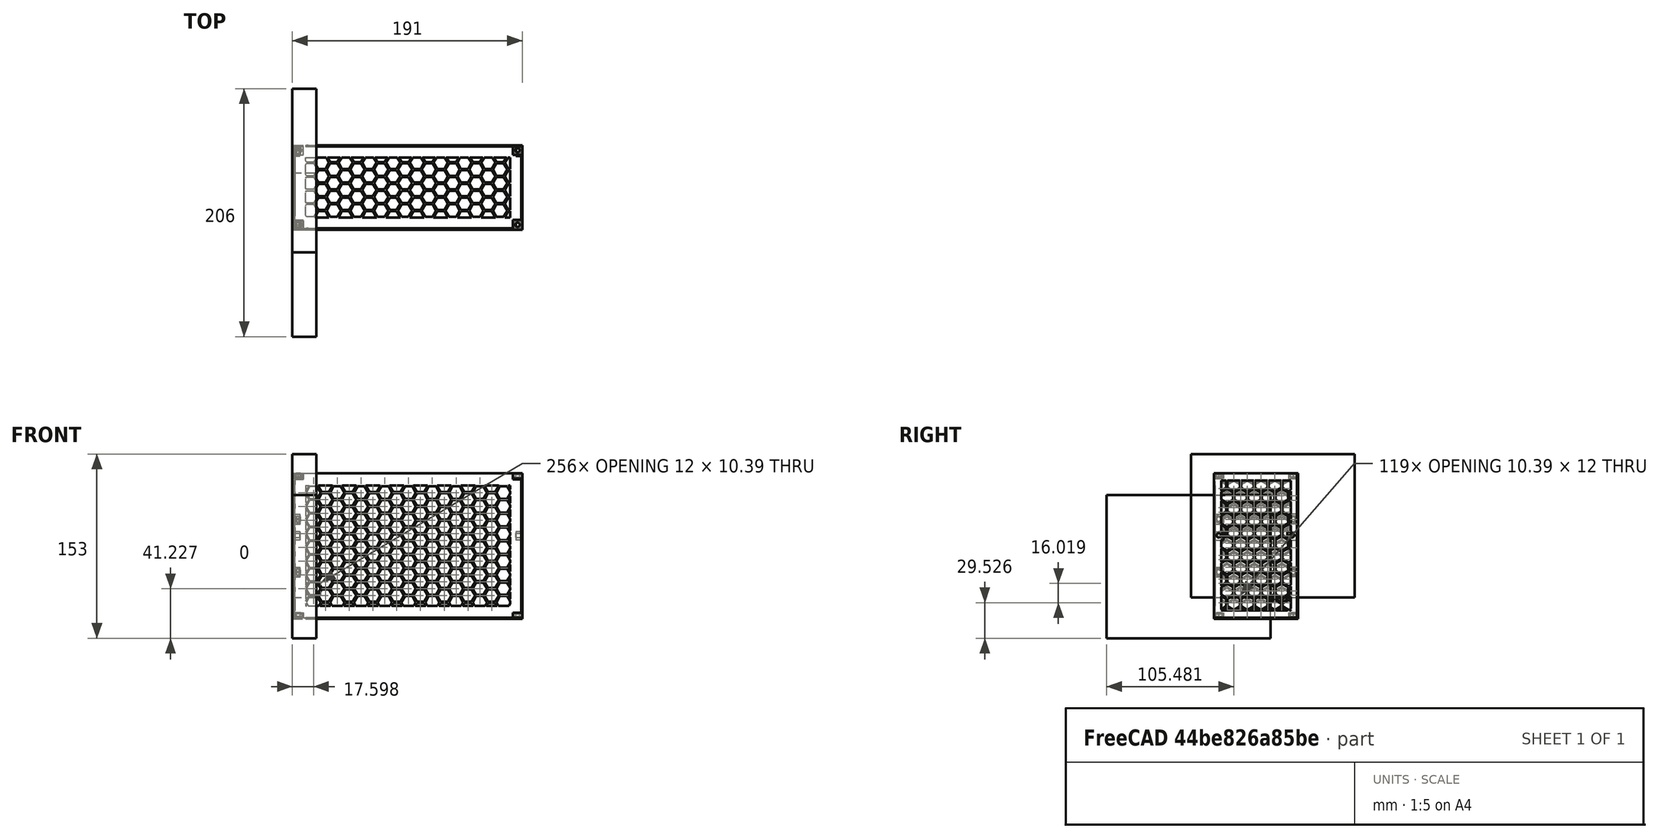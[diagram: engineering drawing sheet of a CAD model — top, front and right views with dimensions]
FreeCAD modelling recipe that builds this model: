
FCSTD DOCUMENT  (FreeCAD 0.18R4 (GitTag))
Label: tapas
License: All rights reserved
LicenseURL: http://en.wikipedia.org/wiki/All_rights_reserved
objects: Part::Box×56, Part::Cut×56, Part::MultiFuse×28, Part::Cylinder×25, Part::Prism×12, Part::Feature×9, Part::MultiCommon×3
note: 189 computed .brp shape members not serialized (recipe doc carries the construction recipe); baked Part::Feature solids carry a one-line shape summary decoded from their .brp

FEATURE [Part::Box] Box031  label="placa002"
  AttacherType = Attacher::AttachEngine3D
  Height = 108
  Length = 1
  Placement = pos=(-89,25,-221) rot=(0,0,1;0rad)
  Width = 58
FEATURE [Part::Box] Box032  label="placa003"
  AttacherType = Attacher::AttachEngine3D
  Height = 108
  Length = 1
  Placement = pos=(-89,25,-221) rot=(0,0,1;0rad)
  Width = 58
FEATURE [Part::Box] Box021  label="Cube017"
  AttacherType = Attacher::AttachEngine3D
  Height = 4.2
  Length = 7
  Placement = pos=(-88,81,-111.2) rot=(0,0,1;0rad)
  Width = 8
FEATURE [Part::Prism] Prism003
  AttacherType = Attacher::AttachEngine3D
  Circumradius = 3.1
  Height = 2.2
  Placement = pos=(-85,85,-110.2) rot=(0,0,1;0rad)
  Polygon = 6
FEATURE [Part::Prism] Prism002
  AttacherType = Attacher::AttachEngine3D
  Circumradius = 3.1
  Height = 2.2
  Placement = pos=(-85,85,-110.2) rot=(0,0,1;0rad)
  Polygon = 6
FEATURE [Part::Box] Box017  label="izquierda"
  AttacherType = Attacher::AttachEngine3D
  Height = 120
  Length = 1
  Placement = pos=(-89,19,-227) rot=(0,0,1;0rad)
  Width = 70
FEATURE [Part::Box] Box030  label="placa1"
  AttacherType = Attacher::AttachEngine3D
  Height = 120
  Length = 1
  Placement = pos=(-89,19,-227) rot=(0,0,1;0rad)
  Width = 70
FEATURE [Part::Prism] Prism001
  AttacherType = Attacher::AttachEngine3D
  Circumradius = 3.4
  Height = 2.4
  Placement = pos=(-85,23,-110.2) rot=(0,0,1;0.523599rad)
  Polygon = 6
FEATURE [Part::Cut] Cut001001001002003001008002002033001001001001001001001002001001002001045002003017008007002010007002014003017024
  Base = -> Box030
  Tool = -> Box032
FEATURE [Part::Box] Box020  label="Cube016"
  AttacherType = Attacher::AttachEngine3D
  Height = 4.2
  Length = 7
  Placement = pos=(-88,19,-111.2) rot=(0,0,1;0rad)
  Width = 8
FEATURE [Part::Box] Box033  label="corta_medio"
  AttacherType = Attacher::AttachEngine3D
  Height = 108
  Length = 1
  Placement = pos=(-89,25,-221) rot=(0,0,1;0rad)
  Width = 58
FEATURE [Part::Box] Box023  label="Cube019"
  AttacherType = Attacher::AttachEngine3D
  Height = 4.2
  Length = 7
  Placement = pos=(-88,19,-111.2) rot=(0,0,1;0rad)
  Width = 8
FEATURE [Part::Box] Box022  label="Cube018"
  AttacherType = Attacher::AttachEngine3D
  Height = 4.2
  Length = 7
  Placement = pos=(-88,81,-111.2) rot=(0,0,1;0rad)
  Width = 8
FEATURE [Part::Prism] Prism004
  AttacherType = Attacher::AttachEngine3D
  Circumradius = 3.1
  Height = 2.2
  Placement = pos=(-85,23,-110.2) rot=(0,0,1;0rad)
  Polygon = 6
FEATURE [Part::Cylinder] Cylinder013
  Angle = 360
  AttacherType = Attacher::AttachEngine3D
  Height = 10
  Placement = pos=(-85,23,-112) rot=(0,0,1;0rad)
  Radius = 1.8
FEATURE [Part::Cut] Cut001001001002003001008002002033001001001001001001001002001001002001045002003017008007002010007002014003017014
  Base = -> Box023
  Tool = -> Cylinder013
FEATURE [Part::Cylinder] Cylinder012
  Angle = 360
  AttacherType = Attacher::AttachEngine3D
  Height = 10
  Placement = pos=(-85,85,-112) rot=(0,0,1;0rad)
  Radius = 1.8
FEATURE [Part::Cylinder] Cylinder010
  Angle = 360
  AttacherType = Attacher::AttachEngine3D
  Height = 10
  Placement = pos=(-85,23,-112) rot=(0,0,1;0rad)
  Radius = 1.8
FEATURE [Part::Cylinder] Cylinder011
  Angle = 360
  AttacherType = Attacher::AttachEngine3D
  Height = 10
  Placement = pos=(-85,85,-112) rot=(0,0,1;0rad)
  Radius = 1.8
FEATURE [Part::Cut] Cut001001001002003001008002002033001001001001001001001002001001002001045002003017008007002010007002014003017012
  Base = -> Box022
  Tool = -> Cylinder012
FEATURE [Part::Cut] Cut001001001002003001008002002033001001001001001001001002001001002001045002003017008007002010007002014003017013
  Base = -> Cut001001001002003001008002002033001001001001001001001002001001002001045002003017008007002010007002014003017012
  Placement = pos=(0,0,-115.8) rot=(0,0,1;0rad)
  Tool = -> Prism003
FEATURE [Part::Cut] Cut001001001002003001008002002033001001001001001001001002001001002001045002003017008007002010007002014003017010
  Base = -> Box021
  Tool = -> Cylinder011
FEATURE [Part::Cut] Cut001001001002003001008002002033001001001001001001001002001001002001045002003017008007002010007002014003017011
  Base = -> Cut001001001002003001008002002033001001001001001001001002001001002001045002003017008007002010007002014003017010
  Tool = -> Prism002
FEATURE [Part::Cut] Cut001001001002003001008002002033001001001001001001001002001001002001045002003017008007002010007002014003017015
  Base = -> Cut001001001002003001008002002033001001001001001001001002001001002001045002003017008007002010007002014003017014
  Placement = pos=(0,0,-115.8) rot=(0,0,1;0rad)
  Tool = -> Prism004
FEATURE [Part::Cut] Cut001001001002003001008002002033001001001001001001001002001001002001045002003017008007002010007002014003017008
  Base = -> Box020
  Tool = -> Cylinder010
FEATURE [Part::Cut] Cut001001001002003001008002002033001001001001001001001002001001002001045002003017008007002010007002014003017009
  Base = -> Cut001001001002003001008002002033001001001001001001001002001001002001045002003017008007002010007002014003017008
  Tool = -> Prism001
FEATURE [Part::MultiFuse] Fusion007002009027003005008003003006005017002002002002002002002002
  Shapes = -> [Box017,Cut001001001002003001008002002033001001001001001001001002001001002001045002003017008007002010007002014003017009]
FEATURE [Part::MultiFuse] Fusion007002009027003005008003003006005017002002002002002002002003
  Shapes = -> [Fusion007002009027003005008003003006005017002002002002002002002002,Cut001001001002003001008002002033001001001001001001001002001001002001045002003017008007002010007002014003017011]
FEATURE [Part::MultiFuse] Fusion007002009027003005008003003006005017002002002002002002002004
  Shapes = -> [Fusion007002009027003005008003003006005017002002002002002002002003,Cut001001001002003001008002002033001001001001001001001002001001002001045002003017008007002010007002014003017013]
FEATURE [Part::MultiFuse] Fusion007002009027003005008003003006005017002002002002002002002005  label="lateral_izquierdo"
  Shapes = -> [Fusion007002009027003005008003003006005017002002002002002002002004,Cut001001001002003001008002002033001001001001001001001002001001002001045002003017008007002010007002014003017015]
FEATURE [Part::Feature] Cut001003  label="panal_simple_6_1"
  Placement = pos=(-88,1,-5) rot=(0,1,0;1.5708rad)
  shape: bbox 2 x 250 x 250 mm, 2959 faces, 324 solids (baked)
FEATURE [Part::Cut] Cut
  Base = -> Box032
  Tool = -> Cut001003
FEATURE [Part::MultiFuse] Fusion
  Shapes = -> [Cut001001001002003001008002002033001001001001001001001002001001002001045002003017008007002010007002014003017024,Cut]
FEATURE [Part::Box] Box039  label="Cube022"
  AttacherType = Attacher::AttachEngine3D
  Height = 4.2
  Length = 7
  Placement = pos=(-88,19,-111.2) rot=(0,0,1;0rad)
  Width = 8
FEATURE [Part::Cylinder] Cylinder024
  Angle = 360
  AttacherType = Attacher::AttachEngine3D
  Height = 210
  Placement = pos=(-100,23,-158.5) rot=(0,1,0;1.5708rad)
  Radius = 1.8
FEATURE [Part::Cylinder] Cylinder018
  Angle = 360
  AttacherType = Attacher::AttachEngine3D
  Height = 10
  Placement = pos=(-85,23,-112) rot=(0,0,1;0rad)
  Radius = 1.8
FEATURE [Part::Prism] Prism007
  AttacherType = Attacher::AttachEngine3D
  Circumradius = 3.1
  Height = 2.2
  Placement = pos=(-85,23,-110.2) rot=(0,0,1;0rad)
  Polygon = 6
FEATURE [Part::Cylinder] Cylinder023
  Angle = 360
  AttacherType = Attacher::AttachEngine3D
  Height = 10
  Placement = pos=(-85,23,-112) rot=(0,0,1;0rad)
  Radius = 1.8
FEATURE [Part::Box] Box041  label="Cube023"
  AttacherType = Attacher::AttachEngine3D
  Height = 150
  Length = 10
  Placement = pos=(-90,88,-257) rot=(0,0,1;0rad)
  Width = 10
FEATURE [Part::Cylinder] Cylinder019
  Angle = 360
  AttacherType = Attacher::AttachEngine3D
  Height = 10
  Placement = pos=(-85,23,-112) rot=(0,0,1;0rad)
  Radius = 1.8
FEATURE [Part::Box] Box042  label="placa004"
  AttacherType = Attacher::AttachEngine3D
  Height = 108
  Length = 1
  Placement = pos=(-89,25,-221) rot=(0,0,1;0rad)
  Width = 58
FEATURE [Part::Cylinder] Cylinder016
  Angle = 360
  AttacherType = Attacher::AttachEngine3D
  Height = 10
  Placement = pos=(-85,23,-112) rot=(0,0,1;0rad)
  Radius = 1.8
FEATURE [Part::Box] Box043  label="Cube024"
  AttacherType = Attacher::AttachEngine3D
  Height = 4.2
  Length = 7
  Placement = pos=(-88,81,-111.2) rot=(0,0,1;0rad)
  Width = 8
FEATURE [Part::Box] Box053  label="pestania002"
  AttacherType = Attacher::AttachEngine3D
  Height = 7
  Length = 1
  Placement = pos=(100,19,-162.5) rot=(0,0,1;0rad)
  Width = 7
FEATURE [Part::Box] Box046  label="Cube028"
  AttacherType = Attacher::AttachEngine3D
  Height = 120
  Length = 190
  Placement = pos=(-89,88,-227) rot=(0,0,1;0rad)
  Width = 1
FEATURE [Part::Box] Box044  label="Cube026"
  AttacherType = Attacher::AttachEngine3D
  Height = 3
  Length = 178
  Placement = pos=(6,6,0) rot=(0,0,1;0rad)
  Width = 58
FEATURE [Part::Prism] Prism008
  AttacherType = Attacher::AttachEngine3D
  Circumradius = 3.1
  Height = 2.2
  Placement = pos=(-85,85,-110.2) rot=(0,0,1;0rad)
  Polygon = 6
FEATURE [Part::Prism] Prism009
  AttacherType = Attacher::AttachEngine3D
  Circumradius = 3.1
  Height = 2.2
  Placement = pos=(-85,85,-110.2) rot=(0,0,1;0rad)
  Polygon = 6
FEATURE [Part::Cylinder] Cylinder028
  Angle = 360
  AttacherType = Attacher::AttachEngine3D
  Height = 10
  Placement = pos=(-85,85,-229) rot=(0,0,1;0rad)
  Radius = 1.8
FEATURE [Part::Box] Box054  label="izquierda001"
  AttacherType = Attacher::AttachEngine3D
  Height = 120
  Length = 1
  Placement = pos=(-89,19,-227) rot=(0,0,1;0rad)
  Width = 70
FEATURE [Part::Box] Box048  label="Cube030"
  AttacherType = Attacher::AttachEngine3D
  Height = 4.2
  Length = 7
  Placement = pos=(-88,19,-111.2) rot=(0,0,1;0rad)
  Width = 8
FEATURE [Part::Box] Box058  label="Cube036"
  AttacherType = Attacher::AttachEngine3D
  Height = 5
  Length = 10
  Placement = pos=(93,14,-227.8) rot=(0,0,1;0rad)
  Width = 10
FEATURE [Part::Box] Box059  label="Cube025"
  AttacherType = Attacher::AttachEngine3D
  Height = 4.2
  Length = 7
  Placement = pos=(-88,81,-111.2) rot=(0,0,1;0rad)
  Width = 8
FEATURE [Part::Box] Box052  label="Cube032"
  AttacherType = Attacher::AttachEngine3D
  Height = 4.2
  Length = 7
  Placement = pos=(-88,19,-111.2) rot=(0,0,1;0rad)
  Width = 8
FEATURE [Part::Cut] Cut001001001002003001008002002033001001001001001001001002001001002001045002003017008007002010007002014003017044  label="porta_tornillo_2"
  Base = -> Box052
  Placement = pos=(207,0,-243.5) rot=(0,1,0;1.5708rad)
  Tool = -> Cylinder023
FEATURE [Part::Box] Box060  label="placa005"
  AttacherType = Attacher::AttachEngine3D
  Height = 120
  Length = 1
  Placement = pos=(-89,19,-227) rot=(0,0,1;0rad)
  Width = 70
FEATURE [Part::Box] Box045  label="Cube027"
  AttacherType = Attacher::AttachEngine3D
  Height = 3
  Length = 190
  Width = 70
FEATURE [Part::Cut] Cut001001001002003001008002002033001001001001001001001002001001002001045002003017008007002010007002014003017027  label="marco001"
  Base = -> Box045
  Placement = pos=(-89,19,-107) rot=(0,0,1;0rad)
  Tool = -> Box044
FEATURE [Part::Prism] Prism010
  AttacherType = Attacher::AttachEngine3D
  Circumradius = 3.1
  Height = 2.2
  Placement = pos=(-85,23,-110.2) rot=(0,0,1;0rad)
  Polygon = 6
FEATURE [Part::Prism] Prism006
  AttacherType = Attacher::AttachEngine3D
  Circumradius = 3.1
  Height = 2.2
  Placement = pos=(-85,85,-110.2) rot=(0,0,1;0rad)
  Polygon = 6
FEATURE [Part::Box] Box051  label="Cube031"
  AttacherType = Attacher::AttachEngine3D
  Height = 4.2
  Length = 7
  Placement = pos=(-88,19,-111.2) rot=(0,0,1;0rad)
  Width = 8
FEATURE [Part::Cylinder] Cylinder015
  Angle = 360
  AttacherType = Attacher::AttachEngine3D
  Height = 10
  Placement = pos=(-85,85,-112) rot=(0,0,1;0rad)
  Radius = 1.8
FEATURE [Part::Box] Box061  label="Cube037"
  AttacherType = Attacher::AttachEngine3D
  Height = 4.2
  Length = 7
  Placement = pos=(-88,19,-111.2) rot=(0,0,1;0rad)
  Width = 8
FEATURE [Part::Cut] Cut001001001002003001008002002033001001001001001001001002001001002001045002003017008007002010007002014003017034
  Base = -> Box059
  Tool = -> Cylinder015
FEATURE [Part::Cut] Cut001001001002003001008002002033001001001001001001001002001001002001045002003017008007002010007002014003017056
  Base = -> Box060
  Tool = -> Box042
FEATURE [Part::Box] Box062  label="Cube038"
  AttacherType = Attacher::AttachEngine3D
  Height = 4.2
  Length = 7
  Placement = pos=(-88,19,-111.2) rot=(0,0,1;0rad)
  Width = 8
FEATURE [Part::Cylinder] Cylinder020
  Angle = 360
  AttacherType = Attacher::AttachEngine3D
  Height = 210
  Placement = pos=(-100,84,-158.5) rot=(0,1,0;1.5708rad)
  Radius = 1.8
FEATURE [Part::Box] Box063  label="corta_medio001"
  AttacherType = Attacher::AttachEngine3D
  Height = 108
  Length = 1
  Placement = pos=(-89,25,-221) rot=(0,0,1;0rad)
  Width = 58
FEATURE [Part::Box] Box034  label="Cube020"
  AttacherType = Attacher::AttachEngine3D
  Height = 150
  Length = 10
  Placement = pos=(-90,88,-257) rot=(0,0,1;0rad)
  Width = 10
FEATURE [Part::Box] Box036  label="Cube021"
  AttacherType = Attacher::AttachEngine3D
  Height = 4.2
  Length = 7
  Placement = pos=(-88,81,-111.2) rot=(0,0,1;0rad)
  Width = 8
FEATURE [Part::Cylinder] Cylinder026
  Angle = 360
  AttacherType = Attacher::AttachEngine3D
  Height = 10
  Placement = pos=(-85,23,-229) rot=(0,0,1;0rad)
  Radius = 1.8
FEATURE [Part::Box] Box064  label="Cube039"
  AttacherType = Attacher::AttachEngine3D
  Height = 4.2
  Length = 7
  Placement = pos=(-88,19,-111.2) rot=(0,0,1;0rad)
  Width = 8
FEATURE [Part::Box] Box056  label="Cube034"
  AttacherType = Attacher::AttachEngine3D
  Height = 5
  Length = 10
  Placement = pos=(-91,14,-112) rot=(0,0,1;0rad)
  Width = 10
FEATURE [Part::Cylinder] Cylinder017
  Angle = 360
  AttacherType = Attacher::AttachEngine3D
  Height = 10
  Placement = pos=(-85,85,-112) rot=(0,0,1;0rad)
  Radius = 1.8
FEATURE [Part::Box] Box065  label="Cube040"
  AttacherType = Attacher::AttachEngine3D
  Height = 4.2
  Length = 7
  Placement = pos=(-88,81,-111.2) rot=(0,0,1;0rad)
  Width = 8
FEATURE [Part::Box] Box049  label="pestania"
  AttacherType = Attacher::AttachEngine3D
  Height = 7
  Length = 1
  Placement = pos=(100,80,-162.5) rot=(0,0,1;0rad)
  Width = 7
FEATURE [Part::Cut] Cut001001001002003001008002002033001001001001001001001002001001002001045002003017008007002010007002014003017035
  Base = -> Box036
  Tool = -> Cylinder017
FEATURE [Part::Cut] Cut001001001002003001008002002033001001001001001001001002001001002001045002003017008007002010007002014003017031
  Base = -> Cut001001001002003001008002002033001001001001001001001002001001002001045002003017008007002010007002014003017035
  Tool = -> Prism006
FEATURE [Part::Box] Box038  label="placa006"
  AttacherType = Attacher::AttachEngine3D
  Height = 120
  Length = 1
  Placement = pos=(-89,19,-227) rot=(0,0,1;0rad)
  Width = 70
FEATURE [Part::Box] Box001  label="Cube001"
  AttacherType = Attacher::AttachEngine3D
  Height = 3
  Length = 178
  Placement = pos=(6,6,0) rot=(0,0,1;0rad)
  Width = 58
FEATURE [Part::Cut] Cut001001001002003001008002002033001001001001001001001002001001002001045002003017008007002010007002014003017038
  Base = -> Box039
  Tool = -> Cylinder016
FEATURE [Part::Cut] Cut001001001002003001008002002033001001001001001001001002001001002001045002003017008007002010007002014003017037
  Base = -> Cut001001001002003001008002002033001001001001001001001002001001002001045002003017008007002010007002014003017038
  Tool = -> Prism007
FEATURE [Part::Prism] Prism011
  AttacherType = Attacher::AttachEngine3D
  Circumradius = 3.1
  Height = 2.2
  Placement = pos=(-85,23,-110.2) rot=(0,0,1;0rad)
  Polygon = 6
FEATURE [Part::Box] Box066  label="Cube041"
  AttacherType = Attacher::AttachEngine3D
  Height = 1
  Length = 190
  Placement = pos=(-89,19,-228) rot=(0,0,1;0rad)
  Width = 70
FEATURE [Part::Cylinder] Cylinder029
  Angle = 360
  AttacherType = Attacher::AttachEngine3D
  Height = 10
  Placement = pos=(-85,23,-112) rot=(0,0,1;0rad)
  Radius = 1.8
FEATURE [Part::Cut] Cut001001001002003001008002002033001001001001001001001002001001002001045002003017008007002010007002014003017055
  Base = -> Box064
  Tool = -> Cylinder029
FEATURE [Part::Cylinder] Cylinder030
  Angle = 360
  AttacherType = Attacher::AttachEngine3D
  Height = 10
  Placement = pos=(-85,85,-112) rot=(0,0,1;0rad)
  Radius = 1.8
FEATURE [Part::Box] Box057  label="Cube035"
  AttacherType = Attacher::AttachEngine3D
  Height = 5
  Length = 10
  Placement = pos=(93,14,-112) rot=(0,0,1;0rad)
  Width = 10
FEATURE [Part::Box] Box037  label="izquierda003"
  AttacherType = Attacher::AttachEngine3D
  Height = 120
  Length = 1
  Placement = pos=(-89,19,-227) rot=(0,0,1;0rad)
  Width = 70
FEATURE [Part::MultiFuse] Fusion007002009027003005008003003006005017002002002002002002002013
  Shapes = -> [Box037,Cut001001001002003001008002002033001001001001001001001002001001002001045002003017008007002010007002014003017037]
FEATURE [Part::Box] Box047  label="Cube029"
  AttacherType = Attacher::AttachEngine3D
  Height = 4.2
  Length = 7
  Placement = pos=(-88,19,-111.2) rot=(0,0,1;0rad)
  Width = 8
FEATURE [Part::Cut] Cut001001001002003001008002002033001001001001001001001002001001002001045002003017008007002010007002014003017039
  Base = -> Box047
  Placement = pos=(23.2,61,-243.5) rot=(0,1,0;1.5708rad)
  Tool = -> Cylinder018
FEATURE [Part::Cylinder] Cylinder031
  Angle = 360
  AttacherType = Attacher::AttachEngine3D
  Height = 10
  Placement = pos=(-85,23,-112) rot=(0,0,1;0rad)
  Radius = 1.8
FEATURE [Part::Prism] Prism012
  AttacherType = Attacher::AttachEngine3D
  Circumradius = 3.1
  Height = 2.2
  Placement = pos=(-85,23,-110.2) rot=(0,0,1;0rad)
  Polygon = 6
FEATURE [Part::Cylinder] Cylinder032
  Angle = 360
  AttacherType = Attacher::AttachEngine3D
  Height = 10
  Placement = pos=(97,85,-229) rot=(0,0,1;0rad)
  Radius = 1.8
FEATURE [Part::Prism] Prism005
  AttacherType = Attacher::AttachEngine3D
  Circumradius = 3.1
  Height = 2.2
  Placement = pos=(-85,85,-110.2) rot=(0,0,1;0rad)
  Polygon = 6
FEATURE [Part::Cut] Cut001001001002003001008002002033001001001001001001001002001001002001045002003017008007002010007002014003017033
  Base = -> Cut001001001002003001008002002033001001001001001001001002001001002001045002003017008007002010007002014003017034
  Placement = pos=(0,0,-115.8) rot=(0,0,1;0rad)
  Tool = -> Prism005
FEATURE [Part::Cylinder] Cylinder033
  Angle = 360
  AttacherType = Attacher::AttachEngine3D
  Height = 10
  Placement = pos=(-85,85,-112) rot=(0,0,1;0rad)
  Radius = 1.8
FEATURE [Part::Box] Box050  label="pestania001"
  AttacherType = Attacher::AttachEngine3D
  Height = 7
  Length = 1
  Placement = pos=(-89,80,-162.5) rot=(0,0,1;0rad)
  Width = 7
FEATURE [Part::Box] Box067  label="Cube042"
  AttacherType = Attacher::AttachEngine3D
  Height = 5
  Length = 10
  Placement = pos=(-91,14,-227.8) rot=(0,0,1;0rad)
  Width = 10
FEATURE [Part::Box] Box035  label="placa007"
  AttacherType = Attacher::AttachEngine3D
  Height = 108
  Length = 1
  Placement = pos=(-89,25,-221) rot=(0,0,1;0rad)
  Width = 58
FEATURE [Part::Cut] Cut001001001002003001008002002033001001001001001001001002001001002001045002003017008007002010007002014003017030
  Base = -> Box038
  Tool = -> Box035
FEATURE [Part::Cut] Cut001001001002003001008002002033001001001001001001001002001001002001045002003017008007002010007002014003017059
  Base = -> Box065
  Tool = -> Cylinder030
FEATURE [Part::Cut] Cut001001001002003001008002002033001001001001001001001002001001002001045002003017008007002010007002014003017058
  Base = -> Cut001001001002003001008002002033001001001001001001001002001001002001045002003017008007002010007002014003017059
  Placement = pos=(0,0,-115.8) rot=(0,0,1;0rad)
  Tool = -> Prism008
FEATURE [Part::Cylinder] Cylinder014
  Angle = 360
  AttacherType = Attacher::AttachEngine3D
  Height = 10
  Placement = pos=(-85,23,-112) rot=(0,0,1;0rad)
  Radius = 1.8
FEATURE [Part::Cut] Cut001001001002003001008002002033001001001001001001001002001001002001045002003017008007002010007002014003017029
  Base = -> Box061
  Tool = -> Cylinder014
FEATURE [Part::Cut] Cut001001001002003001008002002033001001001001001001001002001001002001045002003017008007002010007002014003017036
  Base = -> Cut001001001002003001008002002033001001001001001001001002001001002001045002003017008007002010007002014003017029
  Placement = pos=(0,0,-115.8) rot=(0,0,1;0rad)
  Tool = -> Prism012
FEATURE [Part::Cylinder] Cylinder021
  Angle = 360
  AttacherType = Attacher::AttachEngine3D
  Height = 210
  Placement = pos=(-100,84,-158.5) rot=(0,1,0;1.5708rad)
  Radius = 1.8
FEATURE [Part::Cylinder] Cylinder022
  Angle = 360
  AttacherType = Attacher::AttachEngine3D
  Height = 10
  Placement = pos=(-85,23,-112) rot=(0,0,1;0rad)
  Radius = 1.8
FEATURE [Part::Cut] Cut001001001002003001008002002033001001001001001001001002001001002001045002003017008007002010007002014003017043  label="porta_tornillo_1"
  Base = -> Box051
  Placement = pos=(23.2,0,-243.5) rot=(0,1,0;1.5708rad)
  Tool = -> Cylinder022
FEATURE [Part::Cylinder] Cylinder025
  Angle = 360
  AttacherType = Attacher::AttachEngine3D
  Height = 210
  Placement = pos=(-100,23,-158.5) rot=(0,1,0;1.5708rad)
  Radius = 1.8
FEATURE [Part::MultiFuse] Fusion007002009027003005008003003006005017002002002002002002002015
  Shapes = -> [Fusion007002009027003005008003003006005017002002002002002002002013,Cut001001001002003001008002002033001001001001001001001002001001002001045002003017008007002010007002014003017031]
FEATURE [Part::MultiFuse] Fusion007002009027003005008003003006005017002002002002002002002012
  Shapes = -> [Fusion007002009027003005008003003006005017002002002002002002002015,Cut001001001002003001008002002033001001001001001001001002001001002001045002003017008007002010007002014003017033]
FEATURE [Part::MultiFuse] Fusion007002009027003005008003003006005017002002002002002002002016  label="lateral_izquierdo001"
  Shapes = -> [Fusion007002009027003005008003003006005017002002002002002002002012,Cut001001001002003001008002002033001001001001001001001002001001002001045002003017008007002010007002014003017036]
FEATURE [Part::Cut] Cut001001001002003001008002002033001001001001001001001002001001002001045002003017008007002010007002014003017060
  Base = -> Box043
  Tool = -> Cylinder033
FEATURE [Part::Cut] Cut001001001002003001008002002033001001001001001001001002001001002001045002003017008007002010007002014003017057
  Base = -> Cut001001001002003001008002002033001001001001001001001002001001002001045002003017008007002010007002014003017060
  Tool = -> Prism009
FEATURE [Part::Cut] Cut001001001002003001008002002033001001001001001001001002001001002001045002003017008007002010007002014003017061
  Base = -> Cut001001001002003001008002002033001001001001001001001002001001002001045002003017008007002010007002014003017055
  Placement = pos=(0,0,-115.8) rot=(0,0,1;0rad)
  Tool = -> Prism011
FEATURE [Part::Box] Box040  label="corta_medio002"
  AttacherType = Attacher::AttachEngine3D
  Height = 108
  Length = 1
  Placement = pos=(-89,25,-221) rot=(0,0,1;0rad)
  Width = 58
FEATURE [Part::Cut] Cut001001001002003001008002002033001001001001001001001002001001002001045002003017008007002010007002014003017028
  Base = -> Fusion007002009027003005008003003006005017002002002002002002002016
  Tool = -> Box040
FEATURE [Part::Cylinder] Cylinder027
  Angle = 360
  AttacherType = Attacher::AttachEngine3D
  Height = 10
  Placement = pos=(97,23,-229) rot=(0,0,1;0rad)
  Radius = 1.8
FEATURE [Part::Box] Box  label="Cube"
  AttacherType = Attacher::AttachEngine3D
  Height = 3
  Length = 190
  Width = 70
FEATURE [Part::Cut] Cut001001001002003001008002002033001001001001001001001002001001002001045002003017008007002010007002014003017040  label="marco"
  Base = -> Box
  Placement = pos=(-89,19,-107) rot=(0,0,1;0rad)
  Tool = -> Box001
FEATURE [Part::MultiFuse] Fusion007002009027003005008003003006005017002002002002002002002010
  Shapes = -> [Cut001001001002003001008002002033001001001001001001001002001001002001045002003017008007002010007002014003017056,Cut001001001002003001008002002033001001001001001001001002001001002001045002003017008007002010007002014003017040]
FEATURE [Part::MultiFuse] Fusion007002009027003005008003003006005017002002002002002002002018
  Shapes = -> [Box046,Cut001001001002003001008002002033001001001001001001001002001001002001045002003017008007002010007002014003017039]
FEATURE [Part::MultiFuse] Fusion007002009027003005008003003006005017002002002002002002002014
  Shapes = -> [Cut001001001002003001008002002033001001001001001001001002001001002001045002003017008007002010007002014003017030,Cut001001001002003001008002002033001001001001001001001002001001002001045002003017008007002010007002014003017027]
FEATURE [Part::MultiFuse] Fusion007002009027003005008003003006005017002002002002002002002017  label="placa_lateral_izquierda_panal_alto001"
  Shapes = -> [Fusion007002009027003005008003003006005017002002002002002002002014,Cut001001001002003001008002002033001001001001001001001002001001002001045002003017008007002010007002014003017028]
FEATURE [Part::Cut] Cut001001001002003001008002002033001001001001001001001002001001002001045002003017008007002010007002014003017032  label="placa_lateral_derecha_panal"
  Base = -> Fusion007002009027003005008003003006005017002002002002002002002017
  Placement = pos=(12,0,-334) rot=(0,1,0;3.14159rad)
  Tool = -> Box041
FEATURE [Part::MultiFuse] Fusion007002009027003005008003003006005017002002002002002002002020  label="placa_lateral_derecha_panal_sin_agujero"
  Shapes = -> [Box049,Cut001001001002003001008002002033001001001001001001001002001001002001045002003017008007002010007002014003017032]
FEATURE [Part::Cut] Cut001001001002003001008002002033001001001001001001001002001001002001045002003017008007002010007002014003017041  label="placa_lateral_derecha_panal_1"
  Base = -> Fusion007002009027003005008003003006005017002002002002002002002020
  Tool = -> Cylinder020
FEATURE [Part::MultiFuse] Fusion007002009027003005008003003006005017002002002002002002002022
  Shapes = -> [Box053,Cut001001001002003001008002002033001001001001001001001002001001002001045002003017008007002010007002014003017041]
FEATURE [Part::Cut] Cut001001001002003001008002002033001001001001001001001002001001002001045002003017008007002010007002014003017045  label="placa_lateral_derecha_panal_2"
  Base = -> Fusion007002009027003005008003003006005017002002002002002002002022
  Tool = -> Cylinder025
FEATURE [Part::Box] Box055  label="tapa001"
  AttacherType = Attacher::AttachEngine3D
  Height = 120
  Length = 188
  Placement = pos=(-88,19,-227) rot=(0,0,1;0rad)
  Width = 1
FEATURE [Part::Box] Box068  label="pestania003"
  AttacherType = Attacher::AttachEngine3D
  Height = 7
  Length = 1
  Placement = pos=(-89,19,-162.5) rot=(0,0,1;0rad)
  Width = 7
FEATURE [Part::Cut] Cut001001001002003001008002002033001001001001001001001002001001002001045002003017008007002010007002014003017047
  Base = -> Box055
  Tool = -> Box056
FEATURE [Part::Cut] Cut001001001002003001008002002033001001001001001001001002001001002001045002003017008007002010007002014003017048
  Base = -> Cut001001001002003001008002002033001001001001001001001002001001002001045002003017008007002010007002014003017047
  Tool = -> Box057
FEATURE [Part::Cut] Cut001001001002003001008002002033001001001001001001001002001001002001045002003017008007002010007002014003017049
  Base = -> Cut001001001002003001008002002033001001001001001001001002001001002001045002003017008007002010007002014003017048
  Tool = -> Box058
FEATURE [Part::Cut] Cut001001001002003001008002002033001001001001001001001002001001002001045002003017008007002010007002014003017050  label="placa_base_pura"
  Base = -> Cut001001001002003001008002002033001001001001001001001002001001002001045002003017008007002010007002014003017049
  Tool = -> Box067
FEATURE [Part::MultiFuse] Fusion007002009027003005008003003006005017002002002002002002002027
  Shapes = -> [Cut001001001002003001008002002033001001001001001001001002001001002001045002003017008007002010007002014003017050,Cut001001001002003001008002002033001001001001001001001002001001002001045002003017008007002010007002014003017044]
FEATURE [Part::MultiFuse] Fusion007002009027003005008003003006005017002002002002002002002029  label="placa_base_sin_panal"
  Shapes = -> [Fusion007002009027003005008003003006005017002002002002002002002027,Cut001001001002003001008002002033001001001001001001001002001001002001045002003017008007002010007002014003017043]
FEATURE [Part::Cut] Cut001001001002003001008002002033001001001001001001001002001001002001045002003017008007002010007002014003017063
  Base = -> Box062
  Tool = -> Cylinder031
FEATURE [Part::Cut] Cut001001001002003001008002002033001001001001001001001002001001002001045002003017008007002010007002014003017062
  Base = -> Cut001001001002003001008002002033001001001001001001001002001001002001045002003017008007002010007002014003017063
  Tool = -> Prism010
FEATURE [Part::MultiFuse] Fusion007002009027003005008003003006005017002002002002002002002024
  Shapes = -> [Box054,Cut001001001002003001008002002033001001001001001001001002001001002001045002003017008007002010007002014003017062]
FEATURE [Part::MultiFuse] Fusion007002009027003005008003003006005017002002002002002002002026
  Shapes = -> [Fusion007002009027003005008003003006005017002002002002002002002024,Cut001001001002003001008002002033001001001001001001001002001001002001045002003017008007002010007002014003017057]
FEATURE [Part::MultiFuse] Fusion007002009027003005008003003006005017002002002002002002002023
  Shapes = -> [Fusion007002009027003005008003003006005017002002002002002002002026,Cut001001001002003001008002002033001001001001001001001002001001002001045002003017008007002010007002014003017058]
FEATURE [Part::MultiFuse] Fusion007002009027003005008003003006005017002002002002002002002028  label="lateral_izquierdo002"
  Shapes = -> [Fusion007002009027003005008003003006005017002002002002002002002023,Cut001001001002003001008002002033001001001001001001001002001001002001045002003017008007002010007002014003017061]
FEATURE [Part::Cut] Cut001001001002003001008002002033001001001001001001001002001001002001045002003017008007002010007002014003017025
  Base = -> Fusion007002009027003005008003003006005017002002002002002002002028
  Tool = -> Box063
FEATURE [Part::MultiFuse] Fusion007002009027003005008003003006005017002002002002002002002011  label="placa_lateral_izquierda_panal_alto"
  Shapes = -> [Fusion007002009027003005008003003006005017002002002002002002002010,Cut001001001002003001008002002033001001001001001001001002001001002001045002003017008007002010007002014003017025]
FEATURE [Part::Cut] Cut001001001002003001008002002033001001001001001001001002001001002001045002003017008007002010007002014003017026  label="placa_lateral_izquierda_panal"
  Base = -> Fusion007002009027003005008003003006005017002002002002002002002011
  Tool = -> Box034
FEATURE [Part::MultiFuse] Fusion007002009027003005008003003006005017002002002002002002002021  label="placa_lateral_izquierda_panal_sin_agujero"
  Shapes = -> [Cut001001001002003001008002002033001001001001001001001002001001002001045002003017008007002010007002014003017026,Box050]
FEATURE [Part::Cut] Cut001001001002003001008002002033001001001001001001001002001001002001045002003017008007002010007002014003017042  label="placa_lateral_izquierda_panal_1"
  Base = -> Fusion007002009027003005008003003006005017002002002002002002002021
  Tool = -> Cylinder021
FEATURE [Part::MultiFuse] Fusion007002009027003005008003003006005017002002002002002002002025
  Shapes = -> [Cut001001001002003001008002002033001001001001001001001002001001002001045002003017008007002010007002014003017042,Box068]
FEATURE [Part::Cut] Cut001001001002003001008002002033001001001001001001001002001001002001045002003017008007002010007002014003017046  label="placa_lateral_izquierda_panal_2"
  Base = -> Fusion007002009027003005008003003006005017002002002002002002002025
  Tool = -> Cylinder024
FEATURE [Part::Cut] Cut001001001002003001008002002033001001001001001001001002001001002001045002003017008007002010007002014003017064
  Base = -> Box048
  Placement = pos=(207,61,-243.5) rot=(0,1,0;1.5708rad)
  Tool = -> Cylinder019
FEATURE [Part::MultiFuse] Fusion007002009027003005008003003006005017002002002002002002002019  label="placa_tapa_sin_panal"
  Shapes = -> [Fusion007002009027003005008003003006005017002002002002002002002018,Cut001001001002003001008002002033001001001001001001001002001001002001045002003017008007002010007002014003017064]
FEATURE [Part::Cut] Cut001001001002003001008002002033001001001001001001001002001001002001045002003017008007002010007002014003017051
  Base = -> Box066
  Tool = -> Cylinder026
FEATURE [Part::Cut] Cut001001001002003001008002002033001001001001001001001002001001002001045002003017008007002010007002014003017052
  Base = -> Cut001001001002003001008002002033001001001001001001001002001001002001045002003017008007002010007002014003017051
  Tool = -> Cylinder027
FEATURE [Part::Cut] Cut001001001002003001008002002033001001001001001001001002001001002001045002003017008007002010007002014003017053
  Base = -> Cut001001001002003001008002002033001001001001001001001002001001002001045002003017008007002010007002014003017052
  Tool = -> Cylinder028
FEATURE [Part::Cut] Cut001001001002003001008002002033001001001001001001001002001001002001045002003017008007002010007002014003017054  label="tapa_atras_sin_panal"
  Base = -> Cut001001001002003001008002002033001001001001001001001002001001002001045002003017008007002010007002014003017053
  Tool = -> Cylinder032
FEATURE [Part::Feature] Cut001001001002003001008002002033001001001001001001001002001001002001045002003017008007002010007002014003017065  label="panal_simple_6_002"
  shape: bbox 250 x 250 x 2 mm, 2959 faces, 324 solids (baked)
FEATURE [Part::Box] Box069  label="Cube043"
  AttacherType = Attacher::AttachEngine3D
  Height = 100
  Length = 170
  Placement = pos=(29,200,-1) rot=(1,0,0;1.5708rad)
  Width = 1
FEATURE [Part::MultiCommon] Common
  Placement = pos=(-108,19,-317) rot=(1,0,0;1.5708rad)
  Shapes = -> [Box069,Cut001001001002003001008002002033001001001001001001001002001001002001045002003017008007002010007002014003017065]
FEATURE [Part::Box] Box070  label="Cube044"
  AttacherType = Attacher::AttachEngine3D
  Height = 100
  Length = 170
  Placement = pos=(29,200,-1) rot=(1,0,0;1.5708rad)
  Width = 1
FEATURE [Part::Feature] Cut001001001002003001008002002033001001001001001001001002001001002001045002003017008007002010007002014003017066  label="panal_simple_6_003"
  shape: bbox 250 x 250 x 2 mm, 2959 faces, 324 solids (baked)
FEATURE [Part::MultiCommon] Common001
  Placement = pos=(-108,88,-317) rot=(1,0,0;1.5708rad)
  Shapes = -> [Box070,Cut001001001002003001008002002033001001001001001001001002001001002001045002003017008007002010007002014003017066]
FEATURE [Part::Cut] Cut001001001002003001008002002033001001001001001001001002001001002001045002003017008007002010007002014003017067  label="placa_base_panal"
  Base = -> Fusion007002009027003005008003003006005017002002002002002002002029
  Tool = -> Common
FEATURE [Part::Cut] Cut001001001002003001008002002033001001001001001001001002001001002001045002003017008007002010007002014003017068  label="placa_tapa_panal"
  Base = -> Fusion007002009027003005008003003006005017002002002002002002002019
  Tool = -> Common001
FEATURE [Part::Box] Box071  label="Cube045"
  AttacherType = Attacher::AttachEngine3D
  Height = 1
  Length = 170
  Placement = pos=(-85,24,-232) rot=(0,0,1;0rad)
  Width = 50
FEATURE [Part::Feature] Cut001001001002003001008002002033001001001001001001001002001001002001045002003017008007002010007002014003017069  label="panal_simple_6_004"
  Placement = pos=(122,1,-232) rot=(0,1,0;3.14159rad)
  shape: bbox 250 x 250 x 2 mm, 2959 faces, 324 solids (baked)
FEATURE [Part::MultiCommon] Common002
  Placement = pos=(6,5,4) rot=(0,0,1;0rad)
  Shapes = -> [Box071,Cut001001001002003001008002002033001001001001001001001002001001002001045002003017008007002010007002014003017069]
FEATURE [Part::Box] Box072  label="Cube046"
  AttacherType = Attacher::AttachEngine3D
  Height = 1
  Length = 170
  Placement = pos=(-79,29,-228) rot=(0,0,1;0rad)
  Width = 50
FEATURE [Part::Cut] Cut001001001002003001008002002033001001001001001001001002001001002001045002003017008007002010007002014003017070
  Base = -> Box072
  Tool = -> Common002
FEATURE [Part::Box] Box073  label="Cube047"
  AttacherType = Attacher::AttachEngine3D
  Height = 1
  Length = 170
  Placement = pos=(-79,29,-228) rot=(0,0,1;0rad)
  Width = 50
FEATURE [Part::Cut] Cut001001001002003001008002002033001001001001001001001002001001002001045002003017008007002010007002014003017071
  Base = -> Cut001001001002003001008002002033001001001001001001001002001001002001045002003017008007002010007002014003017054
  Tool = -> Box073
FEATURE [Part::MultiFuse] Fusion007002009027003005008003003006005017002002002002002002002030  label="tapa_atras_panal_111"
  Shapes = -> [Cut001001001002003001008002002033001001001001001001001002001001002001045002003017008007002010007002014003017071,Cut001001001002003001008002002033001001001001001001001002001001002001045002003017008007002010007002014003017070]
FEATURE [Part::Box] Box074  label="Cube048"
  AttacherType = Attacher::AttachEngine3D
  Height = 2.4
  Length = 24
  Placement = pos=(-85,19.6,-110.2) rot=(0,0,1;0rad)
  Width = 6.8
FEATURE [Part::MultiFuse] Fusion007002009027003005008003003006005017002002002002002002002031
  Placement = pos=(0,0,-0.1) rot=(0,0,1;0rad)
  Shapes = -> [Prism001,Box074]
FEATURE [Part::Cylinder] Cylinder034
  Angle = 360
  AttacherType = Attacher::AttachEngine3D
  Height = 10
  Placement = pos=(-85,23,-112) rot=(0,0,1;0rad)
  Radius = 1.85
FEATURE [Part::Box] Box075  label="Cube049"
  AttacherType = Attacher::AttachEngine3D
  Height = 4.2
  Length = 7
  Placement = pos=(-88,19,-111.2) rot=(0,0,1;0rad)
  Width = 8
FEATURE [Part::Cut] Cut001001001002003001008002002033001001001001001001001002001001002001045002003017008007002010007002014003017072
  Base = -> Box075
  Tool = -> Cylinder034
FEATURE [Part::Box] Box076  label="Cube050"
  AttacherType = Attacher::AttachEngine3D
  Height = 4.2
  Length = 1
  Placement = pos=(-89,19,-111.2) rot=(0,0,1;0rad)
  Width = 8
FEATURE [Part::Feature] Fusion007002009027003005008003003006005017002002002002002002002032001  label="pocket_v1"
  shape: bbox 8 x 8 x 4.2 mm, 27 faces (baked)
FEATURE [Part::Feature] Fusion007002009027003005008003003006005017002002002002002002002032008  label="pocket_v006"
  Placement = pos=(23.6,108,-168) rot=(0.57735,0.57735,0.57735;2.0944rad)
  shape: bbox 4.2 x 8 x 8 mm, 27 faces (baked)
FEATURE [Part::Feature] Fusion007002009027003005008003003006005017002002002002002002002032009  label="pocket_v007"
  Placement = pos=(23.6,108,-212) rot=(0.57735,0.57735,0.57735;2.0944rad)
  shape: bbox 4.2 x 8 x 8 mm, 27 faces (baked)
FEATURE [Part::Feature] Fusion007002009027003005008003003006005017002002002002002002002032010  label="pocket_v008"
  Placement = pos=(23.6,0,-166) rot=(0.57735,-0.57735,0.57735;4.18879rad)
  shape: bbox 4.2 x 8 x 8 mm, 27 faces (baked)
FEATURE [Part::Feature] Fusion007002009027003005008003003006005017002002002002002002002032011  label="pocket_v009"
  Placement = pos=(23.6,0,-122) rot=(0.57735,-0.57735,0.57735;4.18879rad)
  shape: bbox 4.2 x 8 x 8 mm, 27 faces (baked)
FEATURE [Part::Box] Box080  label="Cube054"
  AttacherType = Attacher::AttachEngine3D
  Height = 119
  Length = 20
  Placement = pos=(-90,0,-210) rot=(0,0,1;0rad)
  Width = 136
FEATURE [Part::Box] Box081  label="Cube055"
  AttacherType = Attacher::AttachEngine3D
  Height = 119
  Length = 20
  Placement = pos=(-90,-70,-244) rot=(0,0,1;0rad)
  Width = 136
FEATURE [Part::MultiFuse] Fusion007002009027003005008003003006005017002002002002002002002032013
  Shapes = -> [Box076,Cut001001001002003001008002002033001001001001001001001002001001002001045002003017008007002010007002014003017072]
FEATURE [Part::Cut] Cut001001001002003001008002002033001001001001001001001002001001002001045002003017008007002010007002014003017083  label="pocket_v3"
  Base = -> Fusion007002009027003005008003003006005017002002002002002002002032013
  Tool = -> Fusion007002009027003005008003003006005017002002002002002002002031
